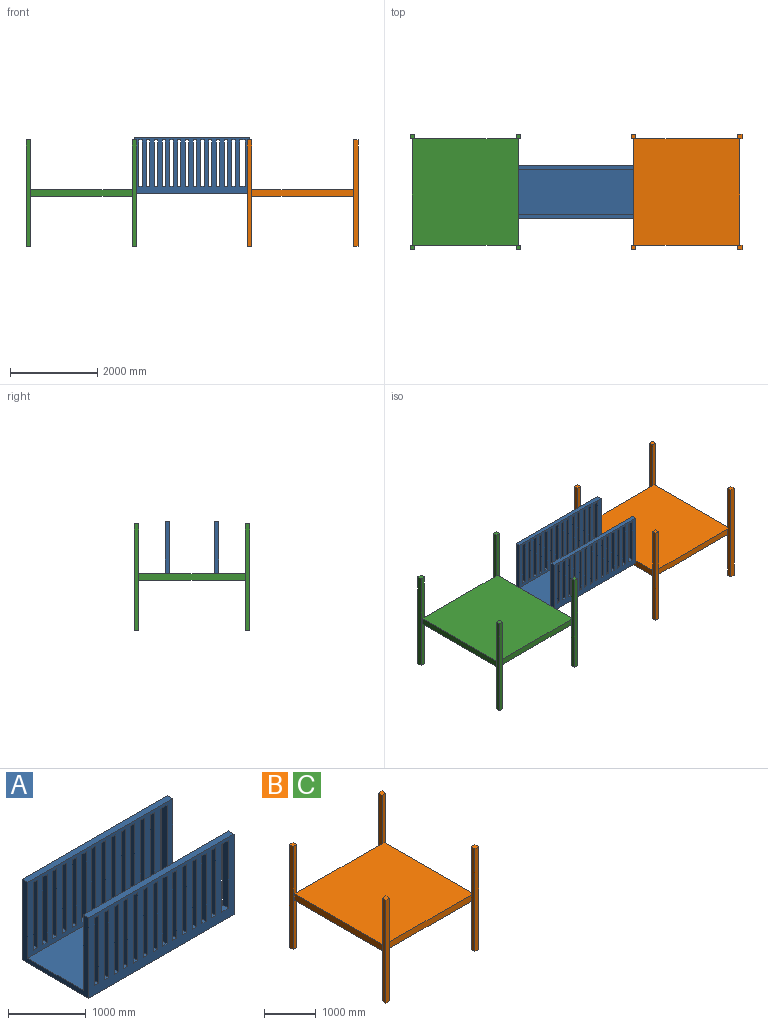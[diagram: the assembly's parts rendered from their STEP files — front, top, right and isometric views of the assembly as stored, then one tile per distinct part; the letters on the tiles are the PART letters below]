
ASSEMBLY  parts=3 mates=2
PART A: 122 faces, bbox 2641.6x1219.2x1270 mm
  f0: plane 1066.8x101.6mm, normal (-1,0,0), area 108386.9mm2, adj f1,f88,f91,f120
  f1: plane 127x101.6mm, normal (0,0,1), area 12903.2mm2, adj f0,f2,f88,f91
  f2: plane 1066.8x101.6mm, normal (1,0,0), area 108386.9mm2, adj f1,f88,f91,f120
  f3: plane 1066.8x101.6mm, normal (-1,0,0), area 108386.9mm2, adj f4,f88,f91,f107
  f4: plane 101.6x76.2mm, normal (0,0,1), area 7741.9mm2, adj f3,f5,f88,f91
  f5: plane 1066.8x101.6mm, normal (1,0,0), area 108386.9mm2, adj f4,f88,f91,f107
  f6: plane 1066.8x101.6mm, normal (-1,0,0), area 108386.9mm2, adj f7,f88,f91,f108
  f7: plane 101.6x76.2mm, normal (0,0,1), area 7741.9mm2, adj f6,f8,f88,f91
  f8: plane 1066.8x101.6mm, normal (1,0,0), area 108386.9mm2, adj f7,f88,f91,f108
  f9: plane 1066.8x101.6mm, normal (-1,0,0), area 108386.9mm2, adj f10,f88,f91,f109
  f10: plane 101.6x76.2mm, normal (0,0,1), area 7741.9mm2, adj f9,f11,f88,f91
  f11: plane 1066.8x101.6mm, normal (1,0,0), area 108386.9mm2, adj f10,f88,f91,f109
  f12: plane 1066.8x101.6mm, normal (-1,0,0), area 108386.9mm2, adj f13,f88,f91,f110
  f13: plane 101.6x76.2mm, normal (0,0,1), area 7741.9mm2, adj f12,f14,f88,f91
  f14: plane 1066.8x101.6mm, normal (1,0,0), area 108386.9mm2, adj f13,f88,f91,f110
  f15: plane 1066.8x101.6mm, normal (-1,0,0), area 108386.9mm2, adj f16,f88,f91,f111
  f16: plane 101.6x76.2mm, normal (0,0,1), area 7741.9mm2, adj f15,f17,f88,f91
  f17: plane 1066.8x101.6mm, normal (1,0,0), area 108386.9mm2, adj f16,f88,f91,f111
  f18: plane 1066.8x101.6mm, normal (-1,0,0), area 108386.9mm2, adj f19,f88,f91,f112
  f19: plane 101.6x76.2mm, normal (0,0,1), area 7741.9mm2, adj f18,f20,f88,f91
  f20: plane 1066.8x101.6mm, normal (1,0,0), area 108386.9mm2, adj f19,f88,f91,f112
  f21: plane 1066.8x101.6mm, normal (-1,0,0), area 108386.9mm2, adj f22,f88,f91,f113
  f22: plane 101.6x76.2mm, normal (0,0,1), area 7741.9mm2, adj f21,f23,f88,f91
  f23: plane 1066.8x101.6mm, normal (1,0,0), area 108386.9mm2, adj f22,f88,f91,f113
  f24: plane 1066.8x101.6mm, normal (-1,0,0), area 108386.9mm2, adj f25,f88,f91,f114
  f25: plane 101.6x76.2mm, normal (0,0,1), area 7741.9mm2, adj f24,f26,f88,f91
  f26: plane 1066.8x101.6mm, normal (1,0,0), area 108386.9mm2, adj f25,f88,f91,f114
  f27: plane 1066.8x101.6mm, normal (-1,0,0), area 108386.9mm2, adj f28,f88,f91,f115
  f28: plane 101.6x76.2mm, normal (0,0,1), area 7741.9mm2, adj f27,f29,f88,f91
  f29: plane 1066.8x101.6mm, normal (1,0,0), area 108386.9mm2, adj f28,f88,f91,f115
  f30: plane 1066.8x101.6mm, normal (-1,0,0), area 108386.9mm2, adj f31,f88,f91,f116
  f31: plane 101.6x76.2mm, normal (0,0,1), area 7741.9mm2, adj f30,f32,f88,f91
  f32: plane 1066.8x101.6mm, normal (1,0,0), area 108386.9mm2, adj f31,f88,f91,f116
  f33: plane 1066.8x101.6mm, normal (-1,0,0), area 108386.9mm2, adj f34,f88,f91,f117
  f34: plane 101.6x76.2mm, normal (0,0,1), area 7741.9mm2, adj f33,f35,f88,f91
  f35: plane 1066.8x101.6mm, normal (1,0,0), area 108386.9mm2, adj f34,f88,f91,f117
  f36: plane 1066.8x101.6mm, normal (-1,0,0), area 108386.9mm2, adj f37,f88,f91,f118
  f37: plane 101.6x76.2mm, normal (0,0,1), area 7741.9mm2, adj f36,f38,f88,f91
  f38: plane 1066.8x101.6mm, normal (1,0,0), area 108386.9mm2, adj f37,f88,f91,f118
  f39: plane 1066.8x101.6mm, normal (-1,0,0), area 108386.9mm2, adj f40,f88,f91,f119
  f40: plane 101.6x76.2mm, normal (0,0,1), area 7741.9mm2, adj f39,f41,f88,f91
  f41: plane 1066.8x101.6mm, normal (1,0,0), area 108386.9mm2, adj f40,f88,f91,f119
  f42: plane 2641.6x1219.2mm, normal (0,0,-1), area 3220638.7mm2, adj f43,f86,f87,f88
  f43: plane 1270x1219.2mm, normal (1,0,0), area 335483.2mm2, adj f42,f87,f88,f89,f90,f91,f106,f121
  f44: plane 1066.8x101.6mm, normal (-1,0,0), area 108386.9mm2, adj f45,f87,f89,f92
  f45: plane 127x101.6mm, normal (0,0,1), area 12903.2mm2, adj f44,f46,f87,f89
  f46: plane 1066.8x101.6mm, normal (1,0,0), area 108386.9mm2, adj f45,f87,f89,f92
  f47: plane 1066.8x101.6mm, normal (-1,0,0), area 108386.9mm2, adj f48,f87,f89,f93
  f48: plane 101.6x76.2mm, normal (0,0,1), area 7741.9mm2, adj f47,f49,f87,f89
  f49: plane 1066.8x101.6mm, normal (1,0,0), area 108386.9mm2, adj f48,f87,f89,f93
  f50: plane 1066.8x101.6mm, normal (-1,0,0), area 108386.9mm2, adj f51,f87,f89,f94
  f51: plane 101.6x76.2mm, normal (0,0,1), area 7741.9mm2, adj f50,f52,f87,f89
  f52: plane 1066.8x101.6mm, normal (1,0,0), area 108386.9mm2, adj f51,f87,f89,f94
  f53: plane 1066.8x101.6mm, normal (-1,0,0), area 108386.9mm2, adj f54,f87,f89,f95
  f54: plane 101.6x76.2mm, normal (0,0,1), area 7741.9mm2, adj f53,f55,f87,f89
  f55: plane 1066.8x101.6mm, normal (1,0,0), area 108386.9mm2, adj f54,f87,f89,f95
  f56: plane 1066.8x101.6mm, normal (-1,0,0), area 108386.9mm2, adj f57,f87,f89,f96
  f57: plane 101.6x76.2mm, normal (0,0,1), area 7741.9mm2, adj f56,f58,f87,f89
  f58: plane 1066.8x101.6mm, normal (1,0,0), area 108386.9mm2, adj f57,f87,f89,f96
  f59: plane 1066.8x101.6mm, normal (-1,0,0), area 108386.9mm2, adj f60,f87,f89,f97
  f60: plane 101.6x76.2mm, normal (0,0,1), area 7741.9mm2, adj f59,f61,f87,f89
  f61: plane 1066.8x101.6mm, normal (1,0,0), area 108386.9mm2, adj f60,f87,f89,f97
  f62: plane 1066.8x101.6mm, normal (-1,0,0), area 108386.9mm2, adj f63,f87,f89,f98
  f63: plane 101.6x76.2mm, normal (0,0,1), area 7741.9mm2, adj f62,f64,f87,f89
  f64: plane 1066.8x101.6mm, normal (1,0,0), area 108386.9mm2, adj f63,f87,f89,f98
  f65: plane 1066.8x101.6mm, normal (-1,0,0), area 108386.9mm2, adj f66,f87,f89,f99
  f66: plane 101.6x76.2mm, normal (0,0,1), area 7741.9mm2, adj f65,f67,f87,f89
  f67: plane 1066.8x101.6mm, normal (1,0,0), area 108386.9mm2, adj f66,f87,f89,f99
  f68: plane 1066.8x101.6mm, normal (-1,0,0), area 108386.9mm2, adj f69,f87,f89,f100
  f69: plane 101.6x76.2mm, normal (0,0,1), area 7741.9mm2, adj f68,f70,f87,f89
  f70: plane 1066.8x101.6mm, normal (1,0,0), area 108386.9mm2, adj f69,f87,f89,f100
  f71: plane 1066.8x101.6mm, normal (-1,0,0), area 108386.9mm2, adj f72,f87,f89,f101
  f72: plane 101.6x76.2mm, normal (0,0,1), area 7741.9mm2, adj f71,f73,f87,f89
  f73: plane 1066.8x101.6mm, normal (1,0,0), area 108386.9mm2, adj f72,f87,f89,f101
  f74: plane 1066.8x101.6mm, normal (-1,0,0), area 108386.9mm2, adj f75,f87,f89,f102
  f75: plane 101.6x76.2mm, normal (0,0,1), area 7741.9mm2, adj f74,f76,f87,f89
  f76: plane 1066.8x101.6mm, normal (1,0,0), area 108386.9mm2, adj f75,f87,f89,f102
  f77: plane 1066.8x101.6mm, normal (-1,0,0), area 108386.9mm2, adj f78,f87,f89,f103
  f78: plane 101.6x76.2mm, normal (0,0,1), area 7741.9mm2, adj f77,f79,f87,f89
  f79: plane 1066.8x101.6mm, normal (1,0,0), area 108386.9mm2, adj f78,f87,f89,f103
  f80: plane 1066.8x101.6mm, normal (-1,0,0), area 108386.9mm2, adj f81,f87,f89,f104
  f81: plane 101.6x76.2mm, normal (0,0,1), area 7741.9mm2, adj f80,f82,f87,f89
  f82: plane 1066.8x101.6mm, normal (1,0,0), area 108386.9mm2, adj f81,f87,f89,f104
  f83: plane 1066.8x101.6mm, normal (-1,0,0), area 108386.9mm2, adj f84,f87,f89,f105
  f84: plane 101.6x76.2mm, normal (0,0,1), area 7741.9mm2, adj f83,f85,f87,f89
  f85: plane 1066.8x101.6mm, normal (1,0,0), area 108386.9mm2, adj f84,f87,f89,f105
  f86: plane 1270x1219.2mm, normal (-1,0,0), area 335483.2mm2, adj f42,f87,f88,f89,f90,f91,f106,f121
  f87: plane 2641.6x1270mm, normal (0,-1,0), area 2162576.3mm2, adj f42,f43,f44,f45,f46,f47,f48,f49
  f88: plane 2641.6x1270mm, normal (0,1,0), area 2162576.3mm2, adj f0,f1,f2,f3,f4,f5,f6,f7
  f89: plane 2641.6x1193.8mm, normal (0,1,0), area 1961286.4mm2, adj f43,f44,f45,f46,f47,f48,f49,f50
  f90: plane 2641.6x1016mm, normal (0,0,1), area 2683865.6mm2, adj f43,f86,f89,f91
  f91: plane 2641.6x1193.8mm, normal (0,-1,0), area 1961286.4mm2, adj f0,f1,f2,f3,f4,f5,f6,f7
  f92: plane 127x101.6mm, normal (0,0,-1), area 12903.2mm2, adj f44,f46,f87,f89
  f93: plane 101.6x76.2mm, normal (0,0,-1), area 7741.9mm2, adj f47,f49,f87,f89
  f94: plane 101.6x76.2mm, normal (0,0,-1), area 7741.9mm2, adj f50,f52,f87,f89
  f95: plane 101.6x76.2mm, normal (0,0,-1), area 7741.9mm2, adj f53,f55,f87,f89
  f96: plane 101.6x76.2mm, normal (0,0,-1), area 7741.9mm2, adj f56,f58,f87,f89
  f97: plane 101.6x76.2mm, normal (0,0,-1), area 7741.9mm2, adj f59,f61,f87,f89
  f98: plane 101.6x76.2mm, normal (0,0,-1), area 7741.9mm2, adj f62,f64,f87,f89
  f99: plane 101.6x76.2mm, normal (0,0,-1), area 7741.9mm2, adj f65,f67,f87,f89
  f100: plane 101.6x76.2mm, normal (0,0,-1), area 7741.9mm2, adj f68,f70,f87,f89
  f101: plane 101.6x76.2mm, normal (0,0,-1), area 7741.9mm2, adj f71,f73,f87,f89
  f102: plane 101.6x76.2mm, normal (0,0,-1), area 7741.9mm2, adj f74,f76,f87,f89
  f103: plane 101.6x76.2mm, normal (0,0,-1), area 7741.9mm2, adj f77,f79,f87,f89
  f104: plane 101.6x76.2mm, normal (0,0,-1), area 7741.9mm2, adj f80,f82,f87,f89
  f105: plane 101.6x76.2mm, normal (0,0,-1), area 7741.9mm2, adj f83,f85,f87,f89
  f106: plane 2641.6x101.6mm, normal (0,0,1), area 268386.6mm2, adj f43,f86,f87,f89
  f107: plane 101.6x76.2mm, normal (0,0,-1), area 7741.9mm2, adj f3,f5,f88,f91
  f108: plane 101.6x76.2mm, normal (0,0,-1), area 7741.9mm2, adj f6,f8,f88,f91
  f109: plane 101.6x76.2mm, normal (0,0,-1), area 7741.9mm2, adj f9,f11,f88,f91
  f110: plane 101.6x76.2mm, normal (0,0,-1), area 7741.9mm2, adj f12,f14,f88,f91
  f111: plane 101.6x76.2mm, normal (0,0,-1), area 7741.9mm2, adj f15,f17,f88,f91
  f112: plane 101.6x76.2mm, normal (0,0,-1), area 7741.9mm2, adj f18,f20,f88,f91
  f113: plane 101.6x76.2mm, normal (0,0,-1), area 7741.9mm2, adj f21,f23,f88,f91
  f114: plane 101.6x76.2mm, normal (0,0,-1), area 7741.9mm2, adj f24,f26,f88,f91
  f115: plane 101.6x76.2mm, normal (0,0,-1), area 7741.9mm2, adj f27,f29,f88,f91
  f116: plane 101.6x76.2mm, normal (0,0,-1), area 7741.9mm2, adj f30,f32,f88,f91
  f117: plane 101.6x76.2mm, normal (0,0,-1), area 7741.9mm2, adj f33,f35,f88,f91
  f118: plane 101.6x76.2mm, normal (0,0,-1), area 7741.9mm2, adj f36,f38,f88,f91
  f119: plane 101.6x76.2mm, normal (0,0,-1), area 7741.9mm2, adj f39,f41,f88,f91
  f120: plane 127x101.6mm, normal (0,0,-1), area 12903.2mm2, adj f0,f2,f88,f91
  f121: plane 2641.6x101.6mm, normal (0,0,1), area 268386.6mm2, adj f43,f86,f88,f91
PART B: 30 faces, bbox 2540x2641.6x2438.4 mm
  f0: plane 2336.8x152.4mm, normal (0,1,0), area 356128.3mm2, adj f3,f5,f21,f26
  f1: plane 2336.8x152.4mm, normal (0,-1,0), area 356128.3mm2, adj f3,f5,f8,f14
  f2: plane 2438.4x152.4mm, normal (1,0,0), area 371612.2mm2, adj f3,f5,f6,f24
  f3: plane 2438.4x2438.4mm, normal (0,0,1), area 5945794.6mm2, adj f0,f1,f2,f4,f6,f12,f23,f24
  f4: plane 2438.4x152.4mm, normal (-1,0,0), area 371612.2mm2, adj f3,f5,f12,f23
  f5: plane 2438.4x2438.4mm, normal (0,0,-1), area 5945794.6mm2, adj f0,f1,f2,f4,f6,f12,f23,f24
  f6: plane 2438.4x101.6mm, normal (0,1,0), area 239999.5mm2, adj f2,f3,f5,f7,f8,f9,f10
  f7: plane 101.6x101.6mm, normal (0,0,1), area 10322.6mm2, adj f6,f8,f10,f11
  f8: plane 2438.4x101.6mm, normal (-1,0,0), area 247741.4mm2, adj f1,f6,f7,f9,f11
  f9: plane 101.6x101.6mm, normal (0,0,-1), area 10322.6mm2, adj f6,f8,f10,f11
  f10: plane 2438.4x101.6mm, normal (1,0,0), area 247741.4mm2, adj f6,f7,f9,f11
  f11: plane 2438.4x101.6mm, normal (0,-1,0), area 247741.4mm2, adj f7,f8,f9,f10
  f12: plane 2438.4x101.6mm, normal (0,1,0), area 239999.5mm2, adj f3,f4,f5,f13,f14,f15,f16
  f13: plane 101.6x101.6mm, normal (0,0,-1), area 10322.6mm2, adj f12,f14,f16,f17
  f14: plane 2438.4x101.6mm, normal (1,0,0), area 247741.4mm2, adj f1,f12,f13,f15,f17
  f15: plane 101.6x101.6mm, normal (0,0,1), area 10322.6mm2, adj f12,f14,f16,f17
  f16: plane 2438.4x101.6mm, normal (-1,0,0), area 247741.4mm2, adj f12,f13,f15,f17
  f17: plane 2438.4x101.6mm, normal (0,-1,0), area 247741.4mm2, adj f13,f14,f15,f16
  f18: plane 2438.4x101.6mm, normal (0,1,0), area 247741.4mm2, adj f19,f20,f21,f22
  f19: plane 2438.4x101.6mm, normal (-1,0,0), area 247741.4mm2, adj f18,f20,f22,f23
  f20: plane 101.6x101.6mm, normal (0,0,1), area 10322.6mm2, adj f18,f19,f21,f23
  f21: plane 2438.4x101.6mm, normal (1,0,0), area 247741.4mm2, adj f0,f18,f20,f22,f23
  f22: plane 101.6x101.6mm, normal (0,0,-1), area 10322.6mm2, adj f18,f19,f21,f23
  f23: plane 2438.4x101.6mm, normal (0,-1,0), area 239999.5mm2, adj f3,f4,f5,f19,f20,f21,f22
  f24: plane 2438.4x101.6mm, normal (0,-1,0), area 239999.5mm2, adj f2,f3,f5,f25,f26,f27,f28
  f25: plane 101.6x101.6mm, normal (0,0,1), area 10322.6mm2, adj f24,f26,f28,f29
  f26: plane 2438.4x101.6mm, normal (-1,0,0), area 247741.4mm2, adj f0,f24,f25,f27,f29
  f27: plane 101.6x101.6mm, normal (0,0,-1), area 10322.6mm2, adj f24,f26,f28,f29
  f28: plane 2438.4x101.6mm, normal (1,0,0), area 247741.4mm2, adj f24,f25,f27,f29
  f29: plane 2438.4x101.6mm, normal (0,1,0), area 247741.4mm2, adj f25,f26,f27,f28
PART C: same geometry as B
PLACE A t=(-95.46,3.39,236.14)mm fixed
PLACE B t=(2444.54,3.39,-373.46)mm
PLACE C t=(-2635.46,3.39,-373.46)mm
MATE fastened A.f86 <-> C.f2  axis (-1,0,0) through (-1416.26,3.39,-297.26)mm
MATE fastened B.f4 <-> A.f43  axis (-1,0,0) through (1225.34,3.39,-297.26)mm
